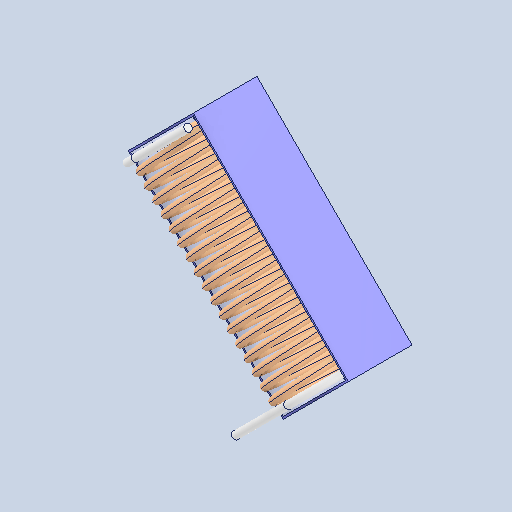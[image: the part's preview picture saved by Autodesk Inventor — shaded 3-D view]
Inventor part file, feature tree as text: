
AUTODESK INVENTOR PART (.ipt)
format: ipt  version: 2025 (Build 290162000, 162)  size: 709,120 bytes
history: native  units: mm
features: sweep x1, other x1
ambient origin geometry x8: Origin, YZ Plane, XZ Plane, XY Plane, X Axis, Y Axis, Z Axis, Center Point
bodies: Solid1 (feature_tree), Solid2 (feature_tree)
feature tree (2):
  sweep  "Sweep9"
  other  "Cut-Extrude1"
